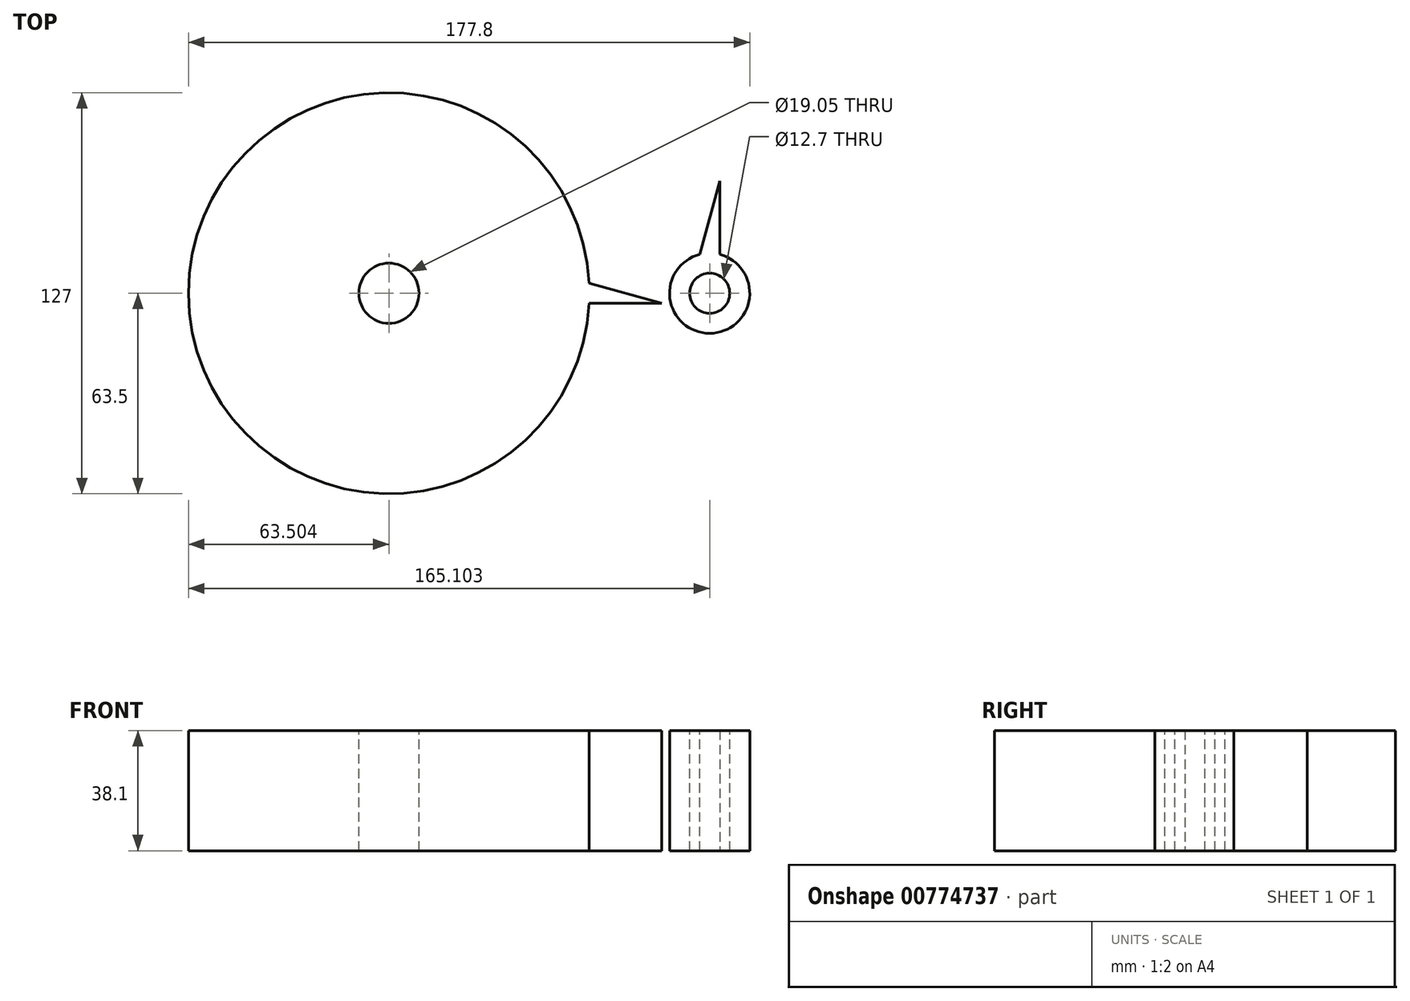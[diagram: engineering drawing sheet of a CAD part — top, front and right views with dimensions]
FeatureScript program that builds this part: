
annotation { "Feature Type Name" : "Feature", "Feature Type Description" : "" }
export const myFeature = defineFeature(function(context is Context, id is Id, definition is map)
    precondition{}
    {
        {
            var Q0;
            Q0=qCreatedBy(makeId("Top.planeOp"),FACE);
            var sketch = newSketch(context, id + "F0", { "sketchPlane" : qUnion([Q0])});
            skCircle(sketch, "E0", {"center": v(-77.24, 0) * mm, "radius": 76.2 * mm, "construction": true});
            skCircle(sketch, "E1", {"center": v(24.36, 0) * mm, "radius": 25.4 * mm, "construction": true});
            skCircle(sketch, "E2", {"center": v(-77.24, 0) * mm, "radius": 86.36 * mm, "construction": true});
            skCircle(sketch, "E3", {"center": v(24.36, 0) * mm, "radius": 35.56 * mm, "construction": true});
            skCircle(sketch, "E4", {"center": v(-77.24, 0) * mm, "radius": 63.5 * mm});
            skCircle(sketch, "E5", {"center": v(24.36, 0) * mm, "radius": 12.7 * mm});
            skSolve(sketch);
        }
        {
            var Q0;
            Q0 = qSketchRegion(id + "F0", true);
            extrude(context, id + "F1", {"entities" : qUnion([Q0]), "depth" : 38.1 * mm, "offsetDistance" : 25.4 * mm});
        }
        {
            var Q0;
            Q0=makeQuery(id+"F1.opExtrude","CAP_FACE",FACE,{"disambiguationData":[OSD([sQuery(id+"F0.wireOp",EDGE,"E4")])],"isStart":false});
            var sketch = newSketch(context, id + "F2", { "sketchPlane" : qUnion([Q0])});
            skLineSegment(sketch, "E6.bottom", {"start": v(-77.24, 3.17) * mm, "end": v(-13.82, 3.17) * mm});
            skLineSegment(sketch, "E6.top", {"start": v(-77.24, -3.18) * mm, "end": v(9.12, -3.18) * mm});
            skLineSegment(sketch, "E6.left", {"start": v(-77.24, 3.18) * mm, "end": v(-77.24, -3.18) * mm});
            skLineSegment(sketch, "E7", {"start": v(9.12, -3.18) * mm, "end": v(-13.82, 3.17) * mm});
            skSolve(sketch);
        }
        {
            var Q0;
            Q0 = qSketchRegion(id + "F2", true);
            extrude(context, id + "F3", {"entities" : qUnion([Q0]), "operationType" : NewBodyOperationType.ADD, "oppositeDirection" : true, "depth" : 38.1 * mm, "offsetDistance" : 25.4 * mm});
        }
        {
            var Q0;
            Q0=makeQuery(id+"F3.boolean.opBoolean","MERGE",FACE,{"derivedFrom":[makeQuery(id+"F1.opExtrude","CAP_FACE",FACE,{"disambiguationData":[OSD([sQuery(id+"F0.wireOp",EDGE,"E4")])],"isStart":false}),makeQuery(id+"F3.opExtrude","CAP_FACE",FACE,{"disambiguationData":[OSD([sQuery(id+"F2.wireOp",EDGE,"E6.bottom"),sQuery(id+"F2.wireOp",EDGE,"E6.top"),sQuery(id+"F2.wireOp",EDGE,"E6.left"),sQuery(id+"F2.wireOp",EDGE,"E6.right")])],"isStart":true})]});
            var sketch = newSketch(context, id + "F4", { "sketchPlane" : qUnion([Q0])});
            skCircle(sketch, "E8", {"center": v(-77.24, 0) * mm, "radius": 17.1 * mm, "construction": true});
            skSolve(sketch);
        }
        {
            var Q0;
            Q0=makeQuery(id+"F1.opExtrude","CAP_FACE",FACE,{"disambiguationData":[OSD([sQuery(id+"F0.wireOp",EDGE,"E5")])],"isStart":false});
            var sketch = newSketch(context, id + "F5", { "sketchPlane" : qUnion([Q0])});
            skLineSegment(sketch, "E9.bottom", {"start": v(27.54, 0) * mm, "end": v(21.19, 0) * mm});
            skLineSegment(sketch, "E9.left", {"start": v(27.54, 0) * mm, "end": v(27.54, 35.56) * mm});
            skLineSegment(sketch, "E9.right", {"start": v(21.19, 0) * mm, "end": v(21.19, 12.3) * mm});
            skLineSegment(sketch, "E10", {"start": v(27.54, 35.56) * mm, "end": v(21.19, 12.3) * mm});
            skPoint(sketch, "E10.endSnap0", {"position": v(21.19, 17.78) * mm});
            skPoint(sketch, "E9.top.end.orphan", {"position": v(21.19, 35.56) * mm});
            skSolve(sketch);
        }
        {
            var Q0;
            Q0 = qSketchRegion(id + "F5", true);
            extrude(context, id + "F6", {"entities" : qUnion([Q0]), "operationType" : NewBodyOperationType.ADD, "oppositeDirection" : true, "depth" : 38.1 * mm, "offsetDistance" : 25.4 * mm});
        }
        {
            var Q0;
            {var subQ0=sQuery(id+"F2.wireOp",EDGE,"E7");var subQ1=sQuery(id+"F2.wireOp",EDGE,"E6.left");var subQ2=sQuery(id+"F2.wireOp",EDGE,"E6.top");var subQ3=sQuery(id+"F2.wireOp",EDGE,"E6.bottom");Q0=makeQuery(id+"FsKQAaiuQrinJzI_2.14.F3.boolean.opBoolean","MERGE",FACE,{"derivedFrom":[makeQuery(id+"FsKQAaiuQrinJzI_2.13.F3.boolean.opBoolean","MERGE",FACE,{"derivedFrom":[makeQuery(id+"FsKQAaiuQrinJzI_2.12.F3.boolean.opBoolean","MERGE",FACE,{"derivedFrom":[makeQuery(id+"FsKQAaiuQrinJzI_2.11.F3.boolean.opBoolean","MERGE",FACE,{"derivedFrom":[makeQuery(id+"FsKQAaiuQrinJzI_2.10.F3.boolean.opBoolean","MERGE",FACE,{"derivedFrom":[makeQuery(id+"FsKQAaiuQrinJzI_2.9.F3.boolean.opBoolean","MERGE",FACE,{"derivedFrom":[makeQuery(id+"FsKQAaiuQrinJzI_2.8.F3.boolean.opBoolean","MERGE",FACE,{"derivedFrom":[makeQuery(id+"FsKQAaiuQrinJzI_2.7.F3.boolean.opBoolean","MERGE",FACE,{"derivedFrom":[makeQuery(id+"FsKQAaiuQrinJzI_2.6.F3.boolean.opBoolean","MERGE",FACE,{"derivedFrom":[makeQuery(id+"FsKQAaiuQrinJzI_2.5.F3.boolean.opBoolean","MERGE",FACE,{"derivedFrom":[makeQuery(id+"FsKQAaiuQrinJzI_2.4.F3.boolean.opBoolean","MERGE",FACE,{"derivedFrom":[makeQuery(id+"FsKQAaiuQrinJzI_2.3.F3.boolean.opBoolean","MERGE",FACE,{"derivedFrom":[makeQuery(id+"FsKQAaiuQrinJzI_2.2.F3.boolean.opBoolean","MERGE",FACE,{"derivedFrom":[makeQuery(id+"FsKQAaiuQrinJzI_2.1.F3.boolean.opBoolean","MERGE",FACE,{"derivedFrom":[makeQuery(id+"F3.boolean.opBoolean","MERGE",FACE,{"derivedFrom":[makeQuery(id+"F1.opExtrude","CAP_FACE",FACE,{"disambiguationData":[OSD([sQuery(id+"F0.wireOp",EDGE,"E4")])],"isStart":false}),makeQuery(id+"F3.opExtrude","CAP_FACE",FACE,{"disambiguationData":[OSD([subQ3,subQ2,subQ1,subQ0])],"isStart":true})]}),makeQuery(id+"FsKQAaiuQrinJzI_2.1.F3.opExtrude","CAP_FACE",FACE,{"disambiguationData":[OSD([subQ3,subQ2,subQ1,subQ0])],"isStart":true})]}),makeQuery(id+"FsKQAaiuQrinJzI_2.2.F3.opExtrude","CAP_FACE",FACE,{"disambiguationData":[OSD([subQ3,subQ2,subQ1,subQ0])],"isStart":true})]}),makeQuery(id+"FsKQAaiuQrinJzI_2.3.F3.opExtrude","CAP_FACE",FACE,{"disambiguationData":[OSD([subQ3,subQ2,subQ1,subQ0])],"isStart":true})]}),makeQuery(id+"FsKQAaiuQrinJzI_2.4.F3.opExtrude","CAP_FACE",FACE,{"disambiguationData":[OSD([subQ3,subQ2,subQ1,subQ0])],"isStart":true})]}),makeQuery(id+"FsKQAaiuQrinJzI_2.5.F3.opExtrude","CAP_FACE",FACE,{"disambiguationData":[OSD([subQ3,subQ2,subQ1,subQ0])],"isStart":true})]}),makeQuery(id+"FsKQAaiuQrinJzI_2.6.F3.opExtrude","CAP_FACE",FACE,{"disambiguationData":[OSD([subQ3,subQ2,subQ1,subQ0])],"isStart":true})]}),makeQuery(id+"FsKQAaiuQrinJzI_2.7.F3.opExtrude","CAP_FACE",FACE,{"disambiguationData":[OSD([subQ3,subQ2,subQ1,subQ0])],"isStart":true})]}),makeQuery(id+"FsKQAaiuQrinJzI_2.8.F3.opExtrude","CAP_FACE",FACE,{"disambiguationData":[OSD([subQ3,subQ2,subQ1,subQ0])],"isStart":true})]}),makeQuery(id+"FsKQAaiuQrinJzI_2.9.F3.opExtrude","CAP_FACE",FACE,{"disambiguationData":[OSD([subQ3,subQ2,subQ1,subQ0])],"isStart":true})]}),makeQuery(id+"FsKQAaiuQrinJzI_2.10.F3.opExtrude","CAP_FACE",FACE,{"disambiguationData":[OSD([subQ3,subQ2,subQ1,subQ0])],"isStart":true})]}),makeQuery(id+"FsKQAaiuQrinJzI_2.11.F3.opExtrude","CAP_FACE",FACE,{"disambiguationData":[OSD([subQ3,subQ2,subQ1,subQ0])],"isStart":true})]}),makeQuery(id+"FsKQAaiuQrinJzI_2.12.F3.opExtrude","CAP_FACE",FACE,{"disambiguationData":[OSD([subQ3,subQ2,subQ1,subQ0])],"isStart":true})]}),makeQuery(id+"FsKQAaiuQrinJzI_2.13.F3.opExtrude","CAP_FACE",FACE,{"disambiguationData":[OSD([subQ3,subQ2,subQ1,subQ0])],"isStart":true})]}),makeQuery(id+"FsKQAaiuQrinJzI_2.14.F3.opExtrude","CAP_FACE",FACE,{"disambiguationData":[OSD([subQ3,subQ2,subQ1,subQ0])],"isStart":true})]});}
            var sketch = newSketch(context, id + "F7", { "sketchPlane" : qUnion([Q0])});
            skCircle(sketch, "E11", {"center": v(-77.24, 0) * mm, "radius": 9.53 * mm});
            skCircle(sketch, "E12", {"center": v(24.36, 0) * mm, "radius": 6.35 * mm});
            skSolve(sketch);
        }
        {
            var Q0;
            Q0 = qSketchRegion(id + "F7", true);
            extrude(context, id + "F8", {"entities" : qUnion([Q0]), "operationType" : NewBodyOperationType.REMOVE, "endBound" : BoundingType.THROUGH_ALL, "oppositeDirection" : true, "depth" : 25.4 * mm, "offsetDistance" : 25.4 * mm});
        }
    });
